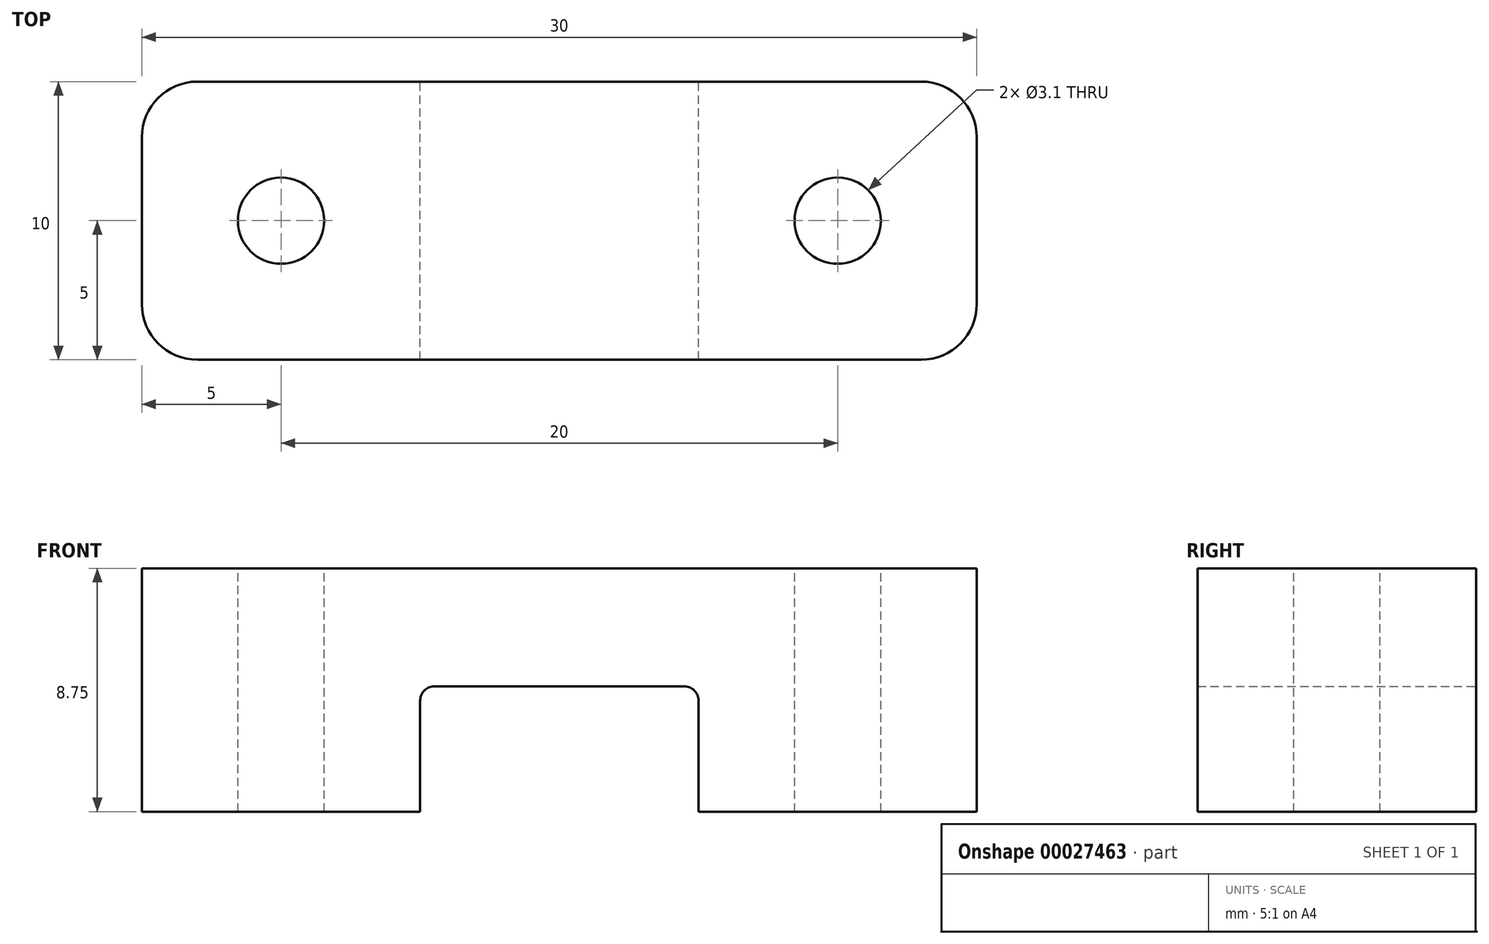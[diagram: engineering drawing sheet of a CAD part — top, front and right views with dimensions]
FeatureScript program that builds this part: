
annotation { "Feature Type Name" : "Feature", "Feature Type Description" : "" }
export const myFeature = defineFeature(function(context is Context, id is Id, definition is map)
    precondition{}
    {
        {
            var Q0;
            Q0=qCreatedBy(makeId("Front.planeOp"),FACE);
            var sketch = newSketch(context, id + "F0", { "sketchPlane" : qUnion([Q0])});
            skLineSegment(sketch, "E0", {"start": v(-15, 0) * mm, "end": v(-5, 0) * mm});
            skLineSegment(sketch, "E1", {"start": v(-5, 0) * mm, "end": v(-5, 4) * mm});
            skLineSegment(sketch, "E2", {"start": v(-4.5, 4.5) * mm, "end": v(4.5, 4.5) * mm});
            skLineSegment(sketch, "E3", {"start": v(5, 4) * mm, "end": v(5, 0) * mm});
            skLineSegment(sketch, "E4", {"start": v(5, 0) * mm, "end": v(15, 0) * mm});
            skLineSegment(sketch, "E5", {"start": v(15, 0) * mm, "end": v(15, 8.75) * mm});
            skLineSegment(sketch, "E6", {"start": v(15, 8.75) * mm, "end": v(-15, 8.75) * mm});
            skLineSegment(sketch, "E7", {"start": v(-15, 8.75) * mm, "end": v(-15, 0) * mm});
            skLineSegment(sketch, "E8", {"start": v(0, 4.5) * mm, "end": v(0, 0) * mm, "construction": true});
            skPoint(sketch, "E9.visualSharp", {"position": v(5, 4.5) * mm});
            skArc(sketch, "E9.filletArc", {"start": v(5, 4) * mm, "mid": v(4.85, 4.35) * mm, "end": v(4.5, 4.5) * mm});
            skPoint(sketch, "E10.visualSharp", {"position": v(-5, 4.5) * mm});
            skArc(sketch, "E10.filletArc", {"start": v(-4.5, 4.5) * mm, "mid": v(-4.85, 4.35) * mm, "end": v(-5, 4) * mm});
            skSolve(sketch);
        }
        {
            var Q0;
            Q0 = qSketchRegion(id + "F0", true);
            extrude(context, id + "F1", {"entities" : qUnion([Q0]), "depth" : 10 * mm, "symmetric" : true});
        }
        {
            var Q0;
            Q0=makeQuery(id+"F1.opExtrude","CAP_EDGE",EDGE,{"disambiguationData":[OSD([sQuery(id+"F0.wireOp",EDGE,"E7")])],"isStart":false});
            var Q1;
            Q1=makeQuery(id+"F1.opExtrude","CAP_EDGE",EDGE,{"disambiguationData":[OSD([sQuery(id+"F0.wireOp",EDGE,"E5")])],"isStart":false});
            var Q2;
            Q2=makeQuery(id+"F1.opExtrude","CAP_EDGE",EDGE,{"disambiguationData":[OSD([sQuery(id+"F0.wireOp",EDGE,"E7")])],"isStart":true});
            var Q3;
            Q3=makeQuery(id+"F1.opExtrude","CAP_EDGE",EDGE,{"disambiguationData":[OSD([sQuery(id+"F0.wireOp",EDGE,"E5")])],"isStart":true});
            fillet(context, id + "F2", {"entities" : qUnion([Q0, Q1, Q2, Q3]), "radius" : 2 * mm, "tangentPropagation" : true, "allowEdgeOverflow" : false});
        }
        {
            var Q0;
            Q0=makeQuery(id+"F1.opExtrude","SWEPT_FACE",FACE,{"disambiguationData":[OSD([sQuery(id+"F0.wireOp",EDGE,"E6")])]});
            var sketch = newSketch(context, id + "F3", { "sketchPlane" : qUnion([Q0])});
            skLineSegment(sketch, "E11", {"start": v(-15, 0) * mm, "end": v(15, 0) * mm, "construction": true});
            skCircle(sketch, "E12", {"center": v(-10, 0) * mm, "radius": 1.55 * mm});
            skCircle(sketch, "E13", {"center": v(10, 0) * mm, "radius": 1.55 * mm});
            skSolve(sketch);
        }
        {
            var Q0;
            Q0 = qSketchRegion(id + "F3", true);
            extrude(context, id + "F4", {"entities" : qUnion([Q0]), "operationType" : NewBodyOperationType.REMOVE, "endBound" : BoundingType.THROUGH_ALL, "oppositeDirection" : true, "depth" : 25 * mm});
        }
    });
